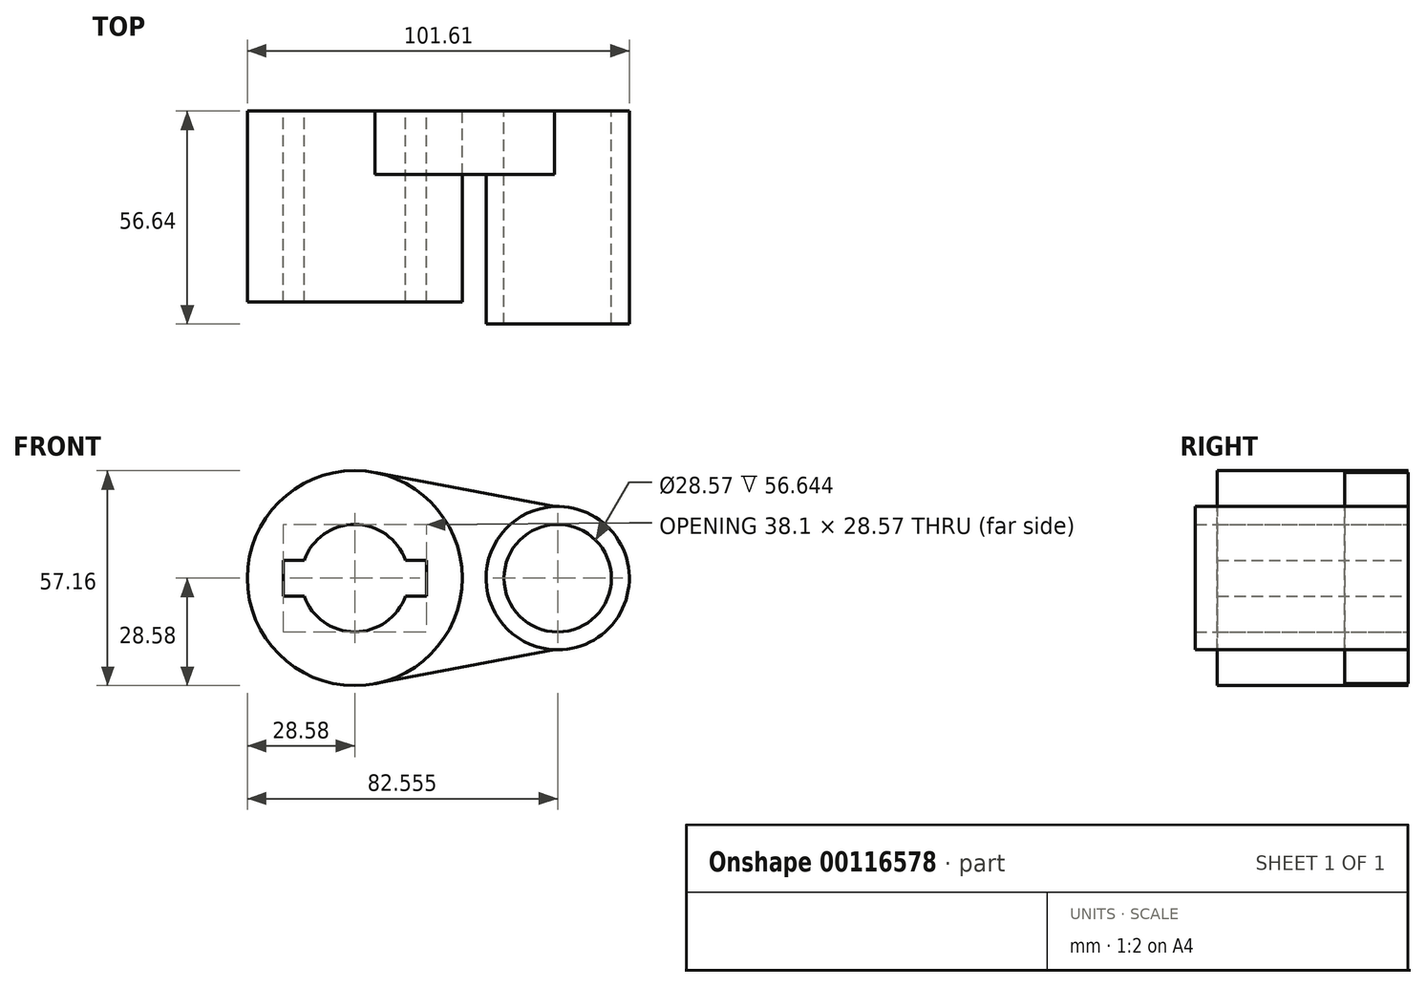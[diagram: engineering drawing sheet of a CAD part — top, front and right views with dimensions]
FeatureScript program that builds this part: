
annotation { "Feature Type Name" : "Feature", "Feature Type Description" : "" }
export const myFeature = defineFeature(function(context is Context, id is Id, definition is map)
    precondition{}
    {
        {
            var Q0;
            Q0=qCreatedBy(makeId("Front.planeOp"),FACE);
            var sketch = newSketch(context, id + "F0", { "sketchPlane" : qUnion([Q0])});
            skCircle(sketch, "E0", {"center": v(0, 0) * mm, "radius": 28.58 * mm});
            skCircle(sketch, "E1", {"center": v(53.98, 0) * mm, "radius": 19.05 * mm});
            skLineSegment(sketch, "E2", {"start": v(5.3, 28.08) * mm, "end": v(53.14, 19.03) * mm});
            skLineSegment(sketch, "E3", {"start": v(5.3, -28.08) * mm, "end": v(53.14, -19.03) * mm});
            skCircle(sketch, "E4", {"center": v(0, 0) * mm, "radius": 14.29 * mm});
            skCircle(sketch, "E5", {"center": v(53.98, 0) * mm, "radius": 14.29 * mm});
            skLineSegment(sketch, "E6.bottom", {"start": v(-19.05, 4.76) * mm, "end": v(19.05, 4.76) * mm});
            skLineSegment(sketch, "E6.top", {"start": v(-19.05, -4.76) * mm, "end": v(19.05, -4.76) * mm});
            skLineSegment(sketch, "E6.left", {"start": v(-19.05, 4.76) * mm, "end": v(-19.05, -4.76) * mm});
            skLineSegment(sketch, "E6.right", {"start": v(19.05, 4.76) * mm, "end": v(19.05, -4.76) * mm});
            skSolve(sketch);
        }
        {
            var Q0;
            {var subQ11=sQuery(id+"F0.wireOp",EDGE,"E6.left");Q0=makeQuery(id+"F0.imprint","IMPRINT",FACE,{"disambiguationData":[TD([[makeQuery(id+"F0.imprint","IMPRINT",EDGE,{"derivedFrom":subQ11}),-1.0]])]});}
            extrude(context, id + "F1", {"entities" : qUnion([Q0]), "depth" : 50.8 * mm});
        }
        {
            var Q0;
            {var subQ0=sQuery(id+"F0.wireOp",EDGE,"E2");Q0=makeQuery(id+"F0.imprint","IMPRINT",FACE,{"disambiguationData":[TD([[makeQuery(id+"F0.imprint","IMPRINT",EDGE,{"derivedFrom":subQ0}),-1.0]])]});}
            extrude(context, id + "F2", {"entities" : qUnion([Q0]), "depth" : 16.9 * mm});
        }
        {
            var Q0;
            Q0=makeQuery(id+"F0.imprint","IMPRINT",FACE,{"disambiguationData":[TD([[makeQuery(id+"F0.imprint","IMPRINT",EDGE,{"derivedFrom":sQuery(id+"F0.wireOp",EDGE,"E5")}),-1.0]])]});
            extrude(context, id + "F3", {"entities" : qUnion([Q0]), "operationType" : NewBodyOperationType.ADD, "depth" : 56.64 * mm});
        }
    });
